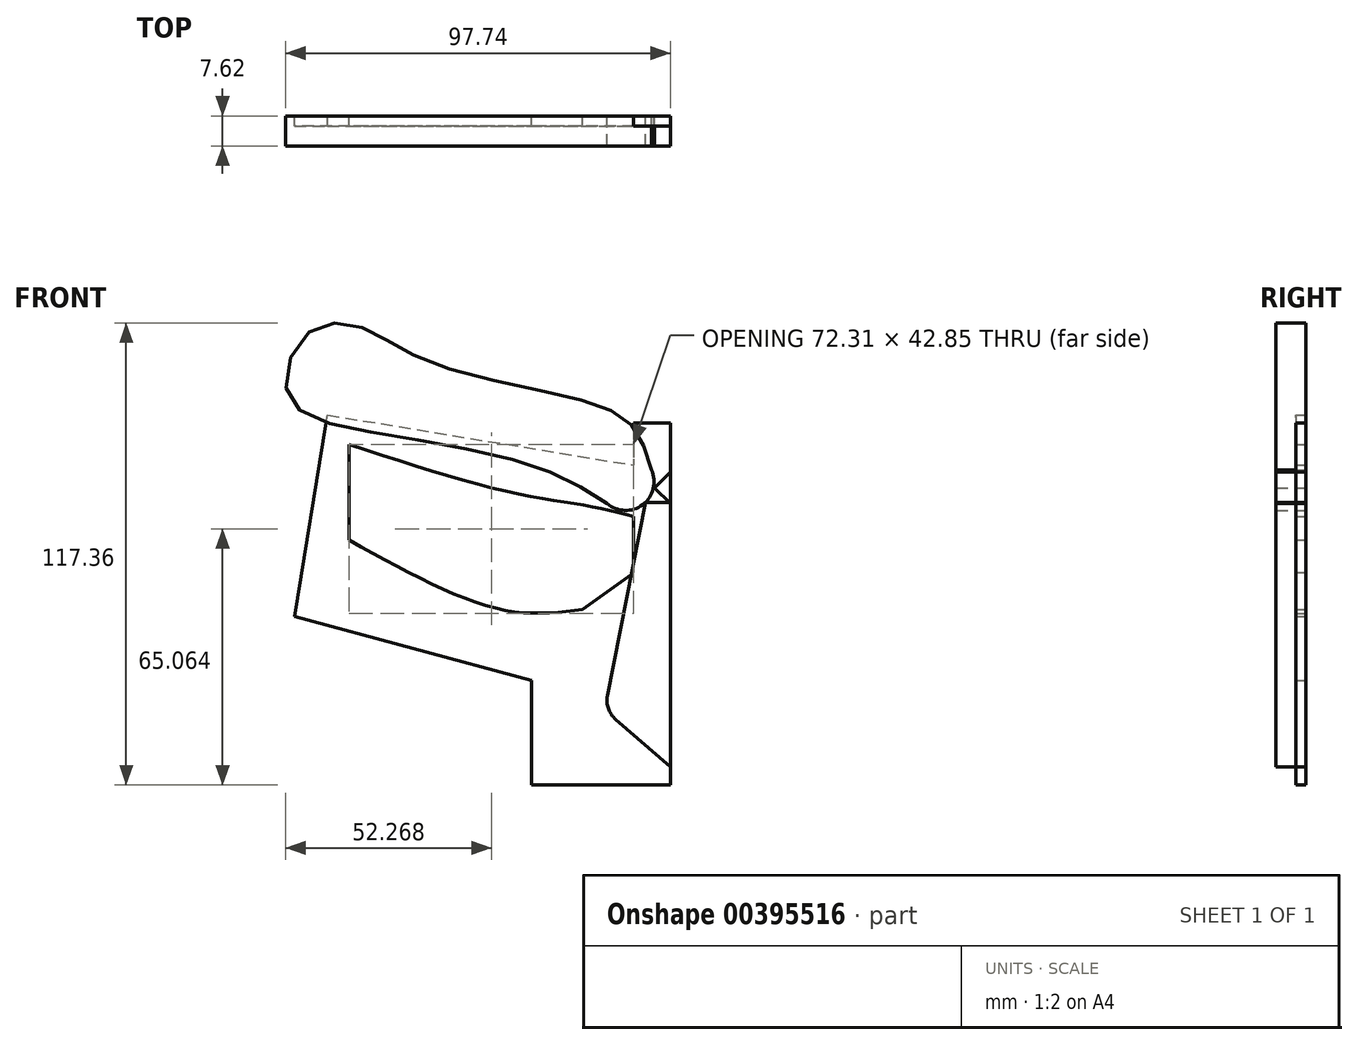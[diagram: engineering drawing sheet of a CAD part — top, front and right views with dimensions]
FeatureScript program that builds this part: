
annotation { "Feature Type Name" : "Feature", "Feature Type Description" : "" }
export const myFeature = defineFeature(function(context is Context, id is Id, definition is map)
    precondition{}
    {
        {
            var Q0;
            Q0=qCreatedBy(makeId("Front.planeOp"),FACE);
            var sketch = newSketch(context, id + "F0", { "sketchPlane" : qUnion([Q0])});
            skLineSegment(sketch, "E0", {"start": v(0, 0) * mm, "end": v(0, 17.78) * mm});
            skLineSegment(sketch, "E1", {"start": v(0, 17.78) * mm, "end": v(-6.35, 17.78) * mm});
            skPoint(sketch, "E2.end.orphan", {"position": v(0, -40.35) * mm});
            skLineSegment(sketch, "E3", {"start": v(-6.35, 17.78) * mm, "end": v(-15.98, -31.24) * mm});
            skLineSegment(sketch, "E4", {"start": v(-13.9, -37.26) * mm, "end": v(0, -49.31) * mm});
            skLineSegment(sketch, "E5", {"start": v(0, 0) * mm, "end": v(0, -49.31) * mm});
            skArc(sketch, "E6", {"start": v(-16.1, 17.62) * mm, "mid": v(-7.01, 17.27) * mm, "end": v(-4.86, 26.1) * mm});
            skFitSpline(sketch, "E7", {"points": [v(-4.86, 26.1) * mm, v(-9.6, 37.18) * mm, v(-23.78, 44.12) * mm, v(-61.67, 53.66) * mm, v(-77.87, 62.05) * mm, v(-91.75, 61.18) * mm, v(-97.25, 45.27) * mm, v(-79.32, 36.3) * mm, v(-36.22, 27.63) * mm, v(-16.1, 17.62) * mm], "startDerivative": vector(-41.38, 146.7) * mm, "endDerivative": vector(151.56, -95.35) * mm});
            skPoint(sketch, "E8.visualSharp", {"position": v(-16.7, -34.85) * mm});
            skArc(sketch, "E8.filletArc", {"start": v(-15.98, -31.24) * mm, "mid": v(-15.75, -34.53) * mm, "end": v(-13.9, -37.26) * mm});
            skSolve(sketch);
        }
        {
            var Q0;
            Q0=qCreatedBy(makeId("Front.planeOp"),FACE);
            var sketch = newSketch(context, id + "F1", { "sketchPlane" : qUnion([Q0])});
            skLineSegment(sketch, "E9.bottom", {"start": v(0, 38.04) * mm, "end": v(-9.31, 38.04) * mm});
            skLineSegment(sketch, "E9.top", {"start": v(0, -53.94) * mm, "end": v(-9.31, -53.94) * mm});
            skLineSegment(sketch, "E9.left", {"start": v(0, 38.04) * mm, "end": v(0, -53.94) * mm});
            skLineSegment(sketch, "E9.right", {"start": v(-9.31, 38.04) * mm, "end": v(-9.31, -53.94) * mm});
            skLineSegment(sketch, "E10.bottom", {"start": v(-9.31, -53.94) * mm, "end": v(-35.35, -53.94) * mm});
            skLineSegment(sketch, "E10.top", {"start": v(-9.31, -18.65) * mm, "end": v(-35.35, -18.65) * mm});
            skLineSegment(sketch, "E10.left", {"start": v(-9.31, -53.94) * mm, "end": v(-9.31, -18.65) * mm});
            skLineSegment(sketch, "E10.right", {"start": v(-35.35, -53.94) * mm, "end": v(-35.35, -18.65) * mm});
            skLineSegment(sketch, "E11", {"start": v(-35.35, -18.65) * mm, "end": v(-9.31, 0) * mm});
            skPoint(sketch, "E12.1.internal.snap0", {"position": v(-22.33, -9.33) * mm});
            skFitSpline(sketch, "E12", {"points": [v(-22.33, -9.33) * mm, v(-43.16, -9.33) * mm, v(-81.63, 8.25) * mm], "startDerivative": vector(-47.42, -6.17) * mm, "endDerivative": vector(-69.86, 38.7) * mm});
            skLineSegment(sketch, "E13", {"start": v(-81.63, 32.55) * mm, "end": v(-81.63, 8.25) * mm});
            skFitSpline(sketch, "E14", {"points": [v(-81.63, 32.55) * mm, v(-40.55, 20.4) * mm, v(-20.89, 16.93) * mm, v(-9.31, 14.32) * mm], "startDerivative": vector(97.94, -31.73) * mm, "endDerivative": vector(46.37, -11.6) * mm});
            skLineSegment(sketch, "E15", {"start": v(-35.35, -27.33) * mm, "end": v(-95.51, -11.13) * mm});
            skLineSegment(sketch, "E16", {"start": v(-95.51, -11.13) * mm, "end": v(-87.13, 40.07) * mm});
            skLineSegment(sketch, "E17", {"start": v(-87.13, 40.07) * mm, "end": v(-9.31, 27.32) * mm});
            skSolve(sketch);
        }
        {
            var Q0;
            Q0=makeQuery(id+"F0.imprint","IMPRINT",FACE,{"disambiguationData":[TD([[makeQuery(id+"F0.imprint","IMPRINT",EDGE,{"derivedFrom":sQuery(id+"F0.wireOp",EDGE,"E6")}),1.0]])]});
            var Q1;
            Q1=makeQuery(id+"F0.imprint","IMPRINT",FACE,{"disambiguationData":[TD([[makeQuery(id+"F0.imprint","IMPRINT",EDGE,{"derivedFrom":sQuery(id+"F0.wireOp",EDGE,"E0")}),1.0]])]});
            extrude(context, id + "F2", {"entities" : qUnion([Q0, Q1]), "depth" : 7.62 * mm});
        }
        {
            var Q0;
            {var subQ3=sQuery(id+"F1.wireOp",EDGE,"E12");Q0=makeQuery(id+"F1.imprint","IMPRINT",FACE,{"disambiguationData":[TD([[makeQuery(id+"F1.imprint","IMPRINT",EDGE,{"derivedFrom":subQ3}),1.0]])]});}
            var Q1;
            {var subQ1=sQuery(id+"F1.wireOp",EDGE,"E10.bottom");Q1=makeQuery(id+"F1.imprint","IMPRINT",FACE,{"disambiguationData":[TD([[makeQuery(id+"F1.imprint","IMPRINT",EDGE,{"derivedFrom":subQ1}),-1.0]])]});}
            var Q2;
            {var subQ0=sQuery(id+"F1.wireOp",EDGE,"E10.top");Q2=makeQuery(id+"F1.imprint","IMPRINT",FACE,{"disambiguationData":[TD([[makeQuery(id+"F1.imprint","IMPRINT",EDGE,{"derivedFrom":subQ0}),-1.0]])]});}
            var Q3;
            {var subQ1=sQuery(id+"F1.wireOp",EDGE,"E9.bottom");Q3=makeQuery(id+"F1.imprint","IMPRINT",FACE,{"disambiguationData":[TD([[makeQuery(id+"F1.imprint","IMPRINT",EDGE,{"derivedFrom":subQ1}),1.0]])]});}
            extrude(context, id + "F3", {"entities" : qUnion([Q0, Q1, Q2, Q3]), "depth" : 2.54 * mm});
        }
        {
            var Q0;
            Q0=qCreatedBy(makeId("Front.planeOp"),FACE);
            var sketch = newSketch(context, id + "F4", { "sketchPlane" : qUnion([Q0])});
            skLineSegment(sketch, "E18", {"start": v(0, 17.56) * mm, "end": v(-4, 21.47) * mm});
            skLineSegment(sketch, "E19", {"start": v(-4, 21.47) * mm, "end": v(0, 25.56) * mm});
            skLineSegment(sketch, "E20", {"start": v(0, 25.56) * mm, "end": v(0, 17.56) * mm});
            skSolve(sketch);
        }
        {
            var Q0;
            Q0 = qSketchRegion(id + "F4", true);
            extrude(context, id + "F5", {"entities" : qUnion([Q0]), "depth" : 7.62 * mm});
        }
    });
